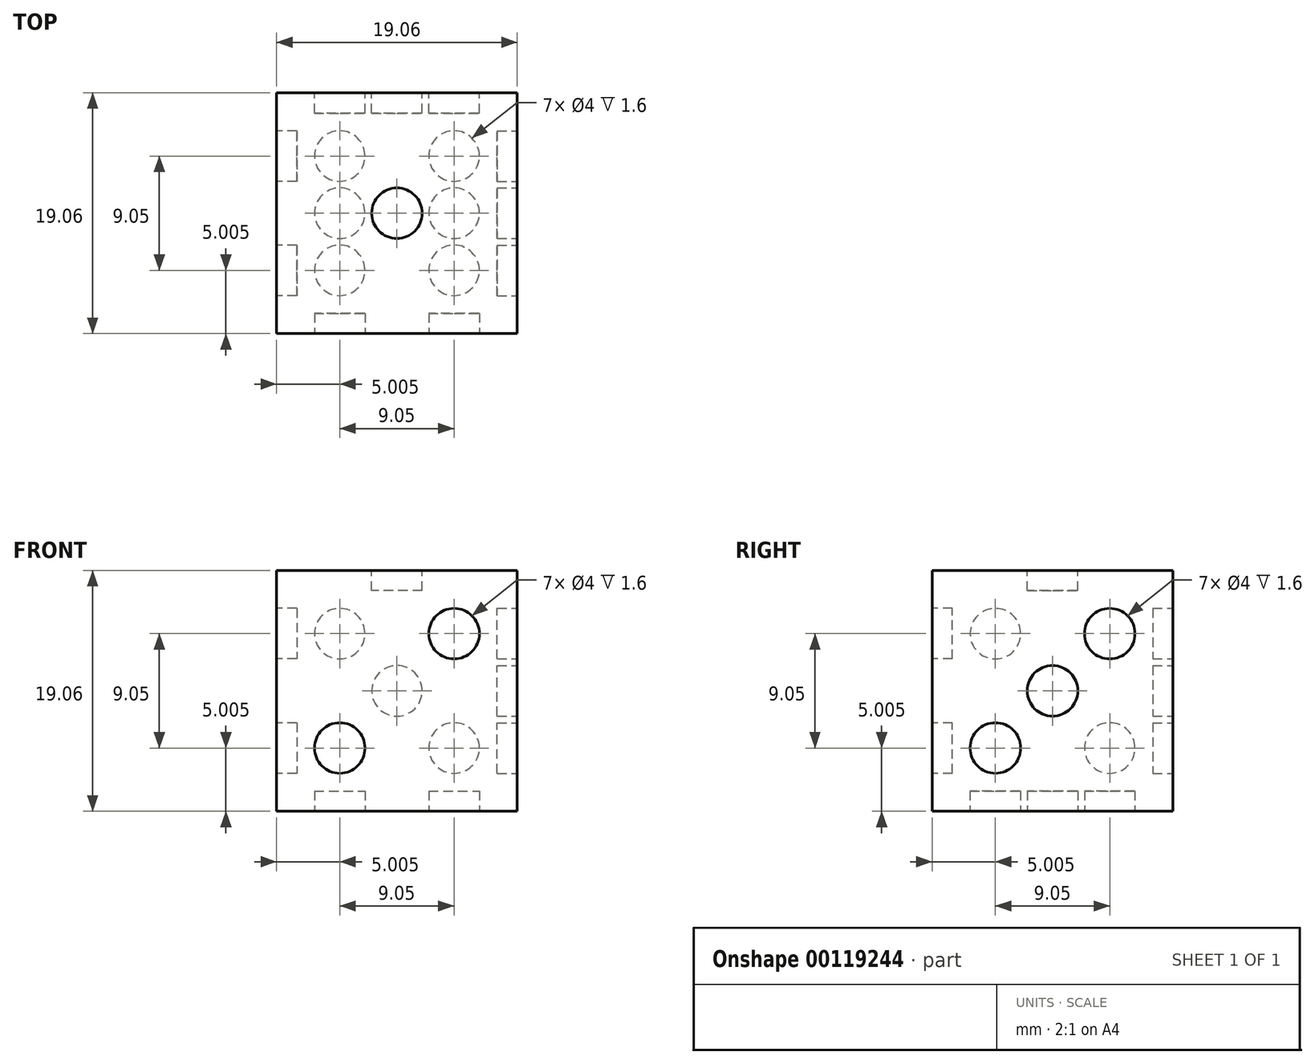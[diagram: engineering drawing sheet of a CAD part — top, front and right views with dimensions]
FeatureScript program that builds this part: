
annotation { "Feature Type Name" : "Feature", "Feature Type Description" : "" }
export const myFeature = defineFeature(function(context is Context, id is Id, definition is map)
    precondition{}
    {
        {
            var Q0;
            Q0=qCreatedBy(makeId("Top.planeOp"),FACE);
            var sketch = newSketch(context, id + "F0", { "sketchPlane" : qUnion([Q0])});
            skLineSegment(sketch, "E0.bottom", {"start": v(9.52, -9.53) * mm, "end": v(-9.53, -9.53) * mm});
            skLineSegment(sketch, "E0.top", {"start": v(9.52, 9.53) * mm, "end": v(-9.53, 9.53) * mm});
            skLineSegment(sketch, "E0.left", {"start": v(9.52, -9.53) * mm, "end": v(9.52, 9.52) * mm});
            skLineSegment(sketch, "E0.right", {"start": v(-9.53, -9.53) * mm, "end": v(-9.53, 9.52) * mm});
            skPoint(sketch, "E0.middle", {"position": v(0, 0) * mm});
            skSolve(sketch);
        }
        {
            var Q0;
            Q0 = qSketchRegion(id + "F0", true);
            extrude(context, id + "F1", {"entities" : qUnion([Q0]), "endBound" : BoundingType.SYMMETRIC, "depth" : 19.05 * mm});
        }
        {
            var Q0;
            Q0=makeQuery(id+"F1.opExtrude","CAP_FACE",FACE,{"disambiguationData":[OSD([sQuery(id+"F0.wireOp",EDGE,"E0.bottom"),sQuery(id+"F0.wireOp",EDGE,"E0.top"),sQuery(id+"F0.wireOp",EDGE,"E0.left"),sQuery(id+"F0.wireOp",EDGE,"E0.right")])],"isStart":false});
            var sketch = newSketch(context, id + "F2", { "sketchPlane" : qUnion([Q0])});
            skCircle(sketch, "E1", {"center": v(0, 0) * mm, "radius": 2 * mm});
            skSolve(sketch);
        }
        {
            var Q0;
            Q0 = qSketchRegion(id + "F2", true);
            extrude(context, id + "F3", {"entities" : qUnion([Q0]), "operationType" : NewBodyOperationType.REMOVE, "oppositeDirection" : true, "depth" : 1.6 * mm});
        }
        {
            var Q0;
            Q0=makeQuery(id+"F1.opExtrude","SWEPT_FACE",FACE,{"disambiguationData":[OSD([sQuery(id+"F0.wireOp",EDGE,"E0.bottom")])]});
            var sketch = newSketch(context, id + "F4", { "sketchPlane" : qUnion([Q0])});
            skCircle(sketch, "E2", {"center": v(4.52, 4.53) * mm, "radius": 2 * mm});
            skCircle(sketch, "E3", {"center": v(-4.53, -4.52) * mm, "radius": 2 * mm});
            skSolve(sketch);
        }
        {
            var Q0;
            Q0 = qSketchRegion(id + "F4", true);
            extrude(context, id + "F5", {"entities" : qUnion([Q0]), "operationType" : NewBodyOperationType.REMOVE, "oppositeDirection" : true, "depth" : 1.6 * mm});
        }
        {
            var Q0;
            Q0=makeQuery(id+"F1.opExtrude","CAP_FACE",FACE,{"disambiguationData":[OSD([sQuery(id+"F0.wireOp",EDGE,"E0.bottom"),sQuery(id+"F0.wireOp",EDGE,"E0.top"),sQuery(id+"F0.wireOp",EDGE,"E0.left"),sQuery(id+"F0.wireOp",EDGE,"E0.right")])],"isStart":true});
            var sketch = newSketch(context, id + "F6", { "sketchPlane" : qUnion([Q0])});
            skCircle(sketch, "E4", {"center": v(-4.53, -4.53) * mm, "radius": 2 * mm});
            skCircle(sketch, "E5.0.1.0", {"center": v(-4.53, 4.53) * mm, "radius": 2 * mm});
            skCircle(sketch, "E5.1.0.0", {"center": v(4.52, -4.53) * mm, "radius": 2 * mm});
            skCircle(sketch, "E5.1.1.0", {"center": v(4.52, 4.53) * mm, "radius": 2 * mm});
            skLineSegment(sketch, "E5.direction1", {"start": v(-4.53, -4.53) * mm, "end": v(4.52, -4.53) * mm, "construction": true});
            skLineSegment(sketch, "E5.direction2", {"start": v(-4.53, -4.53) * mm, "end": v(-4.53, 4.53) * mm, "construction": true});
            skCircle(sketch, "E6", {"center": v(-4.53, 0) * mm, "radius": 2 * mm});
            skCircle(sketch, "E7", {"center": v(4.52, 0) * mm, "radius": 2 * mm});
            skSolve(sketch);
        }
        {
            var Q0;
            Q0 = qSketchRegion(id + "F6", true);
            extrude(context, id + "F7", {"entities" : qUnion([Q0]), "operationType" : NewBodyOperationType.REMOVE, "oppositeDirection" : true, "depth" : 1.6 * mm});
        }
        {
            var Q0;
            Q0=makeQuery(id+"F1.opExtrude","SWEPT_FACE",FACE,{"disambiguationData":[OSD([sQuery(id+"F0.wireOp",EDGE,"E0.top")])]});
            var sketch = newSketch(context, id + "F8", { "sketchPlane" : qUnion([Q0])});
            skCircle(sketch, "E8", {"center": v(-4.52, -4.52) * mm, "radius": 2 * mm});
            skCircle(sketch, "E9.0.1.0", {"center": v(-4.52, 4.53) * mm, "radius": 2 * mm});
            skCircle(sketch, "E9.1.0.0", {"center": v(4.53, -4.52) * mm, "radius": 2 * mm});
            skCircle(sketch, "E9.1.1.0", {"center": v(4.53, 4.53) * mm, "radius": 2 * mm});
            skLineSegment(sketch, "E9.direction1", {"start": v(-4.52, -4.52) * mm, "end": v(4.53, -4.52) * mm, "construction": true});
            skLineSegment(sketch, "E9.direction2", {"start": v(-4.52, -4.52) * mm, "end": v(-4.52, 4.53) * mm, "construction": true});
            skCircle(sketch, "E10", {"center": v(0, 0) * mm, "radius": 2 * mm});
            skSolve(sketch);
        }
        {
            var Q0;
            Q0 = qSketchRegion(id + "F8", true);
            extrude(context, id + "F9", {"entities" : qUnion([Q0]), "operationType" : NewBodyOperationType.REMOVE, "oppositeDirection" : true, "depth" : 1.6 * mm});
        }
        {
            var Q0;
            Q0=makeQuery(id+"F1.opExtrude","SWEPT_FACE",FACE,{"disambiguationData":[OSD([sQuery(id+"F0.wireOp",EDGE,"E0.left")])]});
            var sketch = newSketch(context, id + "F10", { "sketchPlane" : qUnion([Q0])});
            skCircle(sketch, "E11", {"center": v(0, 0) * mm, "radius": 2 * mm});
            skCircle(sketch, "E12", {"center": v(4.52, 4.53) * mm, "radius": 2 * mm});
            skCircle(sketch, "E13", {"center": v(-4.53, -4.52) * mm, "radius": 2 * mm});
            skSolve(sketch);
        }
        {
            var Q0;
            Q0 = qSketchRegion(id + "F10", true);
            extrude(context, id + "F11", {"entities" : qUnion([Q0]), "operationType" : NewBodyOperationType.REMOVE, "oppositeDirection" : true, "depth" : 1.6 * mm});
        }
        {
            var Q0;
            Q0=makeQuery(id+"F1.opExtrude","SWEPT_FACE",FACE,{"disambiguationData":[OSD([sQuery(id+"F0.wireOp",EDGE,"E0.right")])]});
            var sketch = newSketch(context, id + "F12", { "sketchPlane" : qUnion([Q0])});
            skCircle(sketch, "E14", {"center": v(-4.52, -4.52) * mm, "radius": 2 * mm});
            skCircle(sketch, "E15.0.1.0", {"center": v(-4.52, 4.53) * mm, "radius": 2 * mm});
            skCircle(sketch, "E15.1.0.0", {"center": v(4.53, -4.52) * mm, "radius": 2 * mm});
            skCircle(sketch, "E15.1.1.0", {"center": v(4.53, 4.53) * mm, "radius": 2 * mm});
            skLineSegment(sketch, "E15.direction1", {"start": v(-4.52, -4.52) * mm, "end": v(4.53, -4.52) * mm, "construction": true});
            skLineSegment(sketch, "E15.direction2", {"start": v(-4.52, -4.52) * mm, "end": v(-4.52, 4.53) * mm, "construction": true});
            skSolve(sketch);
        }
        {
            var Q0;
            Q0 = qSketchRegion(id + "F12", true);
            extrude(context, id + "F13", {"entities" : qUnion([Q0]), "operationType" : NewBodyOperationType.REMOVE, "oppositeDirection" : true, "depth" : 1.6 * mm});
        }
    });
